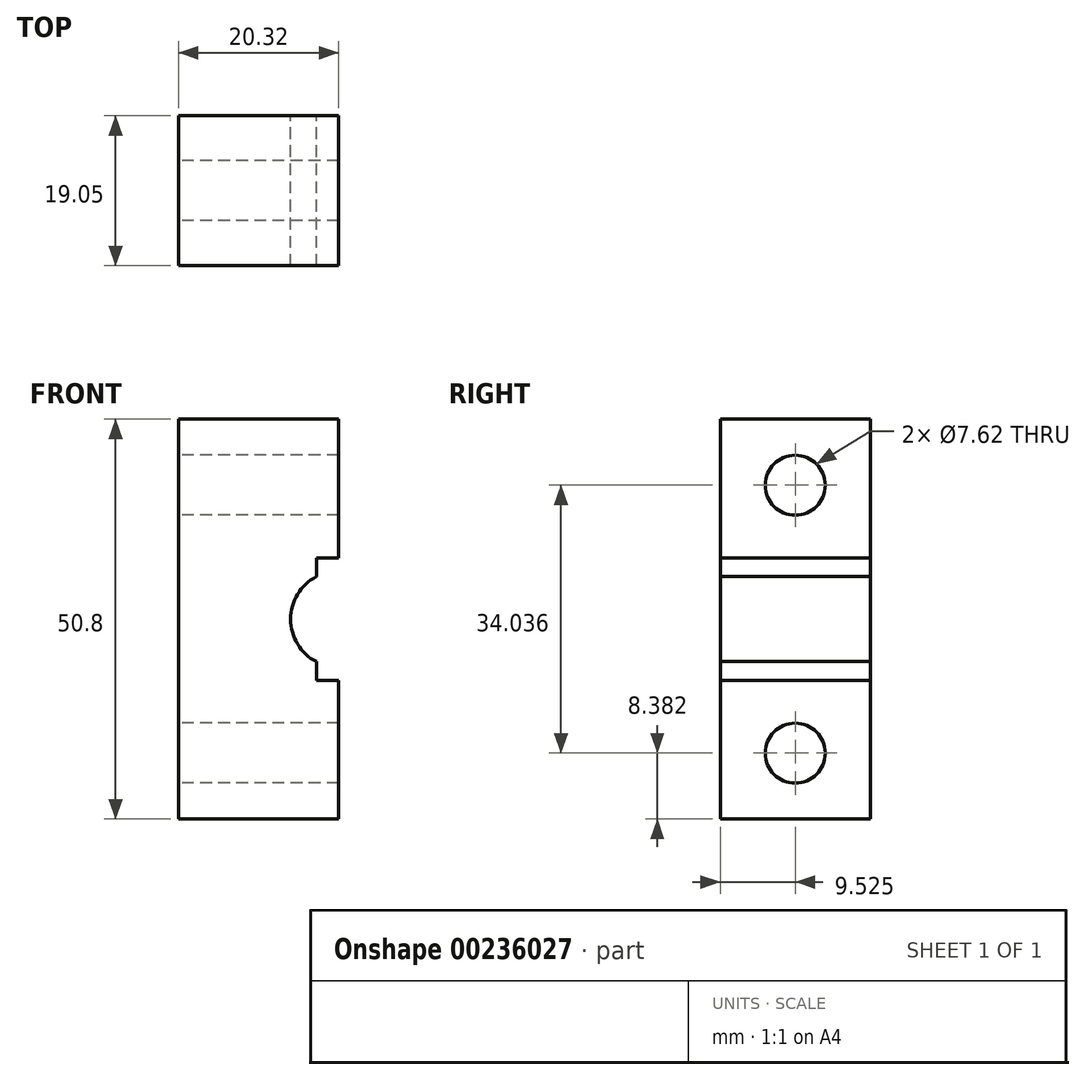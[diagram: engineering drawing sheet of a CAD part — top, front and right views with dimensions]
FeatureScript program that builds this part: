
annotation { "Feature Type Name" : "Feature", "Feature Type Description" : "" }
export const myFeature = defineFeature(function(context is Context, id is Id, definition is map)
    precondition{}
    {
        {
            var Q0;
            Q0=qCreatedBy(makeId("Front.planeOp"),FACE);
            var sketch = newSketch(context, id + "F0", { "sketchPlane" : qUnion([Q0])});
            skLineSegment(sketch, "E0.bottom", {"start": v(-10.16, 25.4) * mm, "end": v(10.16, 25.4) * mm, "construction": true});
            skLineSegment(sketch, "E0.top", {"start": v(-10.16, -25.4) * mm, "end": v(10.16, -25.4) * mm, "construction": true});
            skLineSegment(sketch, "E0.left", {"start": v(-10.16, 25.4) * mm, "end": v(-10.16, -25.4) * mm, "construction": true});
            skLineSegment(sketch, "E0.right", {"start": v(10.16, 25.4) * mm, "end": v(10.16, -25.4) * mm, "construction": true});
            skPoint(sketch, "E0.middle", {"position": v(0, 0) * mm});
            skPoint(sketch, "E1.middle", {"position": v(6.2, 6.6) * mm});
            skLineSegment(sketch, "E2", {"start": v(10.16, 25.4) * mm, "end": v(10.16, 7.8) * mm});
            skLineSegment(sketch, "E3", {"start": v(10.16, 25.4) * mm, "end": v(-10.16, 25.4) * mm});
            skLineSegment(sketch, "E4", {"start": v(-10.16, 25.4) * mm, "end": v(-10.16, -25.4) * mm});
            skLineSegment(sketch, "E5", {"start": v(-10.16, -25.4) * mm, "end": v(10.16, -25.4) * mm});
            skArc(sketch, "E6", {"start": v(7.34, 5.4) * mm, "mid": v(4.07, 0) * mm, "end": v(7.33, -5.4) * mm});
            skLineSegment(sketch, "E7", {"start": v(10.16, -7.8) * mm, "end": v(10.16, -25.4) * mm});
            skLineSegment(sketch, "E8", {"start": v(7.34, 5.4) * mm, "end": v(7.34, 7.8) * mm});
            skPoint(sketch, "E8.endSnap0", {"position": v(6.2, 7.8) * mm});
            skLineSegment(sketch, "E9", {"start": v(7.33, -5.4) * mm, "end": v(7.33, -7.8) * mm});
            skLineSegment(sketch, "E10", {"start": v(7.34, 7.8) * mm, "end": v(10.16, 7.8) * mm});
            skLineSegment(sketch, "E11", {"start": v(7.33, -7.8) * mm, "end": v(10.16, -7.8) * mm});
            skSolve(sketch);
        }
        {
            var Q0;
            Q0 = qSketchRegion(id + "F0", true);
            extrude(context, id + "F1", {"entities" : qUnion([Q0]), "depth" : 19.05 * mm});
        }
        {
            var Q0;
            Q0=makeQuery(id+"F1.opExtrude","SWEPT_FACE",FACE,{"disambiguationData":[OSD([sQuery(id+"F0.wireOp",EDGE,"E4")])]});
            var sketch = newSketch(context, id + "F2", { "sketchPlane" : qUnion([Q0])});
            skPoint(sketch, "E12.endSnap0", {"position": v(9.53, 12.7) * mm});
            skCircle(sketch, "E13", {"center": v(9.53, 17.02) * mm, "radius": 3.81 * mm});
            skCircle(sketch, "E14.MirrorC", {"center": v(9.53, -17.02) * mm, "radius": 3.81 * mm});
            skSolve(sketch);
        }
        {
            var Q0;
            Q0 = qSketchRegion(id + "F2", true);
            extrude(context, id + "F3", {"entities" : qUnion([Q0]), "operationType" : NewBodyOperationType.REMOVE, "oppositeDirection" : true, "depth" : 25.4 * mm});
        }
    });
